# Revit family: Faucet-Valves_and_Controls-KOHLER-BEITOU-K-99869T_1
name_source: partatom
category: Plumbing Fixtures
revit_build: Autodesk Revit 2017 (Build: 20160225_1515(x64)
units: mm (PartAtom-declared; Revit-internal decimal feet)

## family parameters
Cut with Voids When Loaded = No
Host = Face
OmniClass Number = 23.27.31.00
Part Type = Normal
Room Calculation Point = No
Round Connector Dimension = Use Diameter
Shared = No

## types (1)
- CP-Polished Chrome
    ADA Compliant = No
    Assembly Code = D2020
    CW Connection = Yes
    Cold Water Inlet = Cold Water Inlet
    Date Modified = 09/30/2020
    Default Elevation = 36"
    Description = Manda Faucet Series Manda In-Wall Thermostatic 2-way Spool
    Finish = Kohler-Metal-CP-Polished_Chrome
    Flow Rate = 0 GPM
    HW Connection = Yes
    Height = 8 7/16"
    Hot Water Inlet = Hot Water Inlet
    Length = 6 5/16"
    Manufacturer = KOHLER Co.
    Master Format 2014 = 23 09 13.33
    Master Format 2014 Name = Control Valves
    Material = Brass Construction
    Model = K-99869T-CP
    Pressure = 43.51 psi
    Product Name = BEITOU
    Product Page URL = https://www.kohler.com.cn
    Tempered water Outlet 1 = Tempered water Outlet 1
    Tempered water Outlet 2 = Tempered water Outlet 2
    Type = 1
    URL = http://www.kohler.com.cn
    Vent Connection = No
    Waste Connection = No
    Waste Water Outlet = Waste Water Outlet
    WaterSense Certified = No
    Width = 2 15/16"

## geometry (parser evidence)
native form markers: Sweep x4
no freeform markers — native parametric forms only
